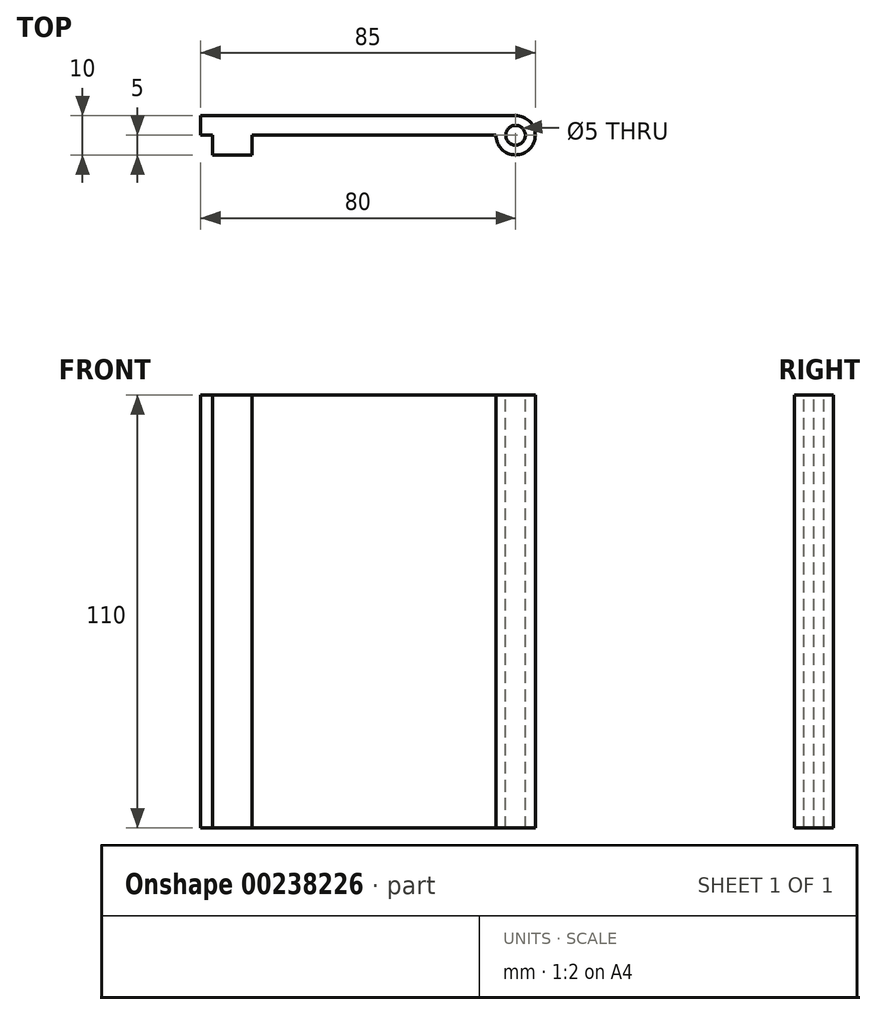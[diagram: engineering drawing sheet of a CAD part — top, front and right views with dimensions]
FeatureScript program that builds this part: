
annotation { "Feature Type Name" : "Feature", "Feature Type Description" : "" }
export const myFeature = defineFeature(function(context is Context, id is Id, definition is map)
    precondition{}
    {
        {
            var Q0;
            Q0=qCreatedBy(makeId("Front.planeOp"),FACE);
            var sketch = newSketch(context, id + "F0", { "sketchPlane" : qUnion([Q0])});
            skLineSegment(sketch, "E0.bottom", {"start": v(0, 110) * mm, "end": v(80, 110) * mm});
            skLineSegment(sketch, "E0.top", {"start": v(0, 0) * mm, "end": v(80, 0) * mm});
            skLineSegment(sketch, "E0.left", {"start": v(0, 110) * mm, "end": v(0, 0) * mm});
            skLineSegment(sketch, "E0.right", {"start": v(80, 110) * mm, "end": v(80, 0) * mm});
            skSolve(sketch);
        }
        {
            var Q0;
            Q0 = qSketchRegion(id + "F0", true);
            extrude(context, id + "F1", {"entities" : qUnion([Q0]), "depth" : 5 * mm});
        }
        {
            var Q0;
            Q0=makeQuery(id+"F1.opExtrude","SWEPT_FACE",FACE,{"disambiguationData":[OSD([sQuery(id+"F0.wireOp",EDGE,"E0.bottom")])]});
            var sketch = newSketch(context, id + "F2", { "sketchPlane" : qUnion([Q0])});
            skCircle(sketch, "E1", {"center": v(80, -5) * mm, "radius": 5 * mm});
            skPoint(sketch, "E2.visualSharp", {"position": v(-1, -12) * mm});
            skLineSegment(sketch, "E3.bottom", {"start": v(3, -5) * mm, "end": v(13, -5) * mm});
            skLineSegment(sketch, "E3.top", {"start": v(3, -10) * mm, "end": v(13, -10) * mm});
            skLineSegment(sketch, "E3.left", {"start": v(3, -5) * mm, "end": v(3, -10) * mm});
            skLineSegment(sketch, "E3.right", {"start": v(13, -5) * mm, "end": v(13, -10) * mm});
            skSolve(sketch);
        }
        {
            var Q0;
            Q0 = qSketchRegion(id + "F2", true);
            var Q1;
            Q1=makeQuery(id+"F1.opExtrude","SWEPT_FACE",FACE,{"disambiguationData":[OSD([sQuery(id+"F0.wireOp",EDGE,"E0.top")])]});
            extrude(context, id + "F3", {"entities" : qUnion([Q0]), "operationType" : NewBodyOperationType.ADD, "endBound" : BoundingType.UP_TO_SURFACE, "oppositeDirection" : true, "endBoundEntityFace" : qUnion([Q1]), "depth" : 25 * mm});
        }
        {
            var Q0;
            Q0=makeQuery(id+"F3.boolean.opBoolean","MERGE",FACE,{"derivedFrom":[makeQuery(id+"F1.opExtrude","SWEPT_FACE",FACE,{"disambiguationData":[OSD([sQuery(id+"F0.wireOp",EDGE,"E0.bottom")])]}),makeQuery(id+"F3.opExtrude","CAP_FACE",FACE,{"disambiguationData":[OSD([sQuery(id+"F2.wireOp",EDGE,"E1")])],"isStart":true})]});
            var sketch = newSketch(context, id + "F4", { "sketchPlane" : qUnion([Q0])});
            skCircle(sketch, "E4", {"center": v(80, -5) * mm, "radius": 2.5 * mm});
            skSolve(sketch);
        }
        {
            var Q0;
            Q0 = qSketchRegion(id + "F4", true);
            extrude(context, id + "F5", {"entities" : qUnion([Q0]), "operationType" : NewBodyOperationType.REMOVE, "endBound" : BoundingType.UP_TO_NEXT, "oppositeDirection" : true, "depth" : 25 * mm});
        }
    });
